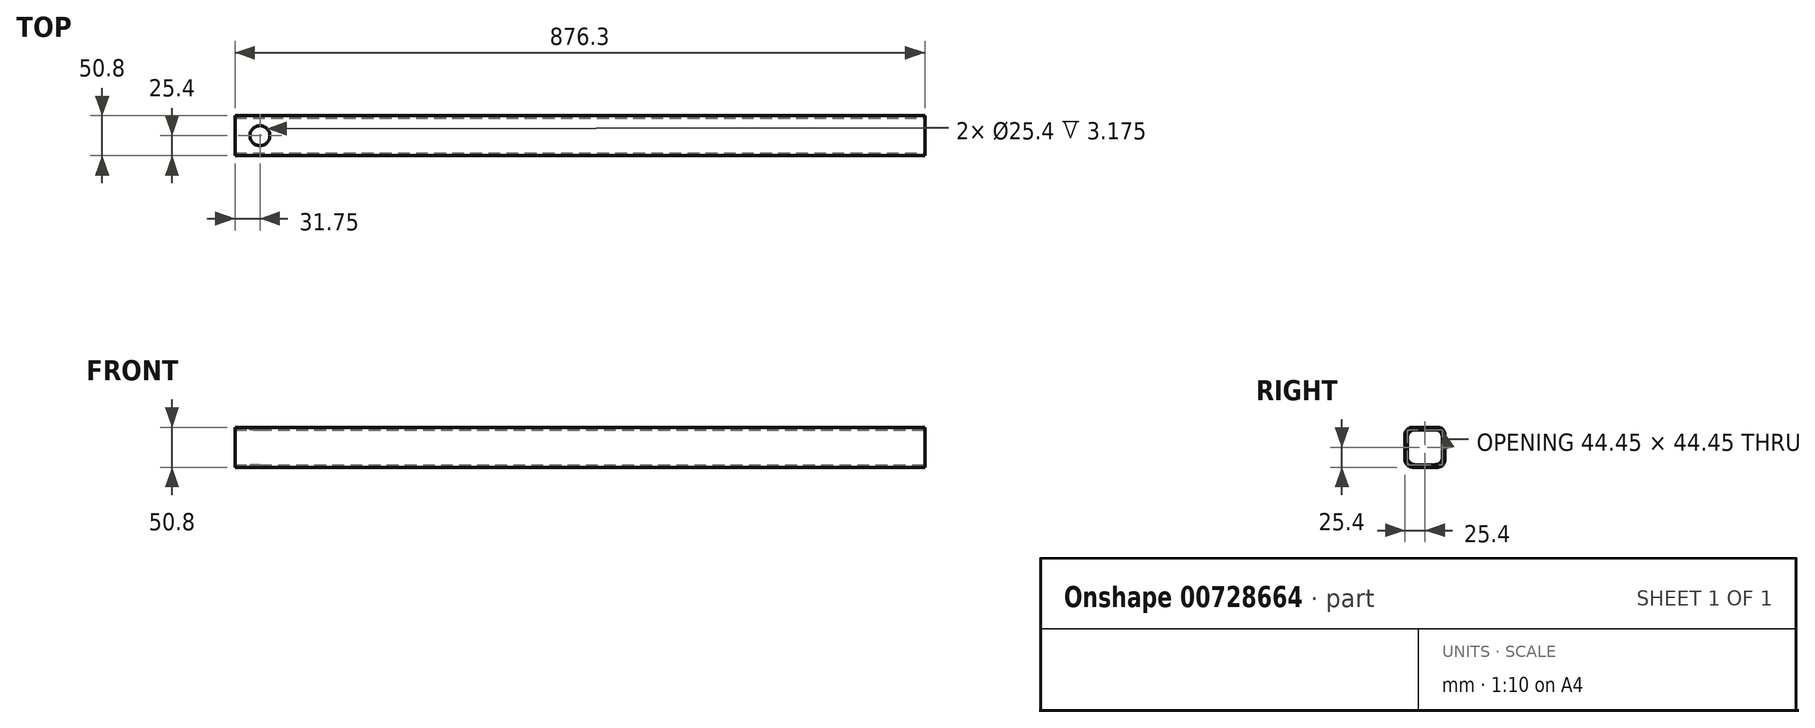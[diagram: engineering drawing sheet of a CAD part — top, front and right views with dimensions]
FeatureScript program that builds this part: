
annotation { "Feature Type Name" : "Feature", "Feature Type Description" : "" }
export const myFeature = defineFeature(function(context is Context, id is Id, definition is map)
    precondition{}
    {
        {
            var Q0;
            Q0=qCreatedBy(makeId("Right.planeOp"),FACE);
            var sketch = newSketch(context, id + "F0", { "sketchPlane" : qUnion([Q0])});
            skLineSegment(sketch, "E0.bottom", {"start": v(0, 0) * mm, "end": v(50.8, 0) * mm});
            skLineSegment(sketch, "E0.top", {"start": v(0, 50.8) * mm, "end": v(50.8, 50.8) * mm});
            skLineSegment(sketch, "E0.left", {"start": v(0, 0) * mm, "end": v(0, 50.8) * mm});
            skLineSegment(sketch, "E0.right", {"start": v(50.8, 0) * mm, "end": v(50.8, 50.8) * mm});
            skSolve(sketch);
        }
        {
            var Q0;
            Q0=qSketchRegion(id+"F0",true);
            extrude(context, id + "F1", {"entities" : qUnion([Q0]), "oppositeDirection" : true, "depth" : 876.3 * mm, "offsetDistance" : 25.4 * mm});
        }
        {
            var Q0;
            Q0=makeQuery(id+"F1.opExtrude","CAP_FACE",FACE,{"disambiguationData":[OSD([sQuery(id+"F0.wireOp",EDGE,"E0.bottom"),sQuery(id+"F0.wireOp",EDGE,"E0.top"),sQuery(id+"F0.wireOp",EDGE,"E0.left"),sQuery(id+"F0.wireOp",EDGE,"E0.right")])],"isStart":true});
            var sketch = newSketch(context, id + "F2", { "sketchPlane" : qUnion([Q0])});
            skLineSegment(sketch, "E1.0", {"start": v(3.17, 47.63) * mm, "end": v(47.63, 47.63) * mm});
            skLineSegment(sketch, "E1.1", {"start": v(3.17, 3.17) * mm, "end": v(3.17, 47.63) * mm});
            skLineSegment(sketch, "E1.2", {"start": v(3.17, 3.17) * mm, "end": v(47.63, 3.17) * mm});
            skLineSegment(sketch, "E1.3", {"start": v(47.63, 3.17) * mm, "end": v(47.63, 47.63) * mm});
            skSolve(sketch);
        }
        {
            var Q0;
            Q0=qSketchRegion(id+"F2",true);
            extrude(context, id + "F3", {"entities" : qUnion([Q0]), "operationType" : NewBodyOperationType.REMOVE, "oppositeDirection" : true, "depth" : 876.3 * mm, "offsetDistance" : 25.4 * mm});
        }
        {
            var Q0;
            Q0=makeQuery(id+"F3.boolean.opBoolean","COPY",EDGE,{"derivedFrom":makeQuery(id+"F3.opExtrude","SWEPT_EDGE",EDGE,{"disambiguationData":[OSD([sQuery(id+"F2.wireOp",EDGE,"E1.1"),sQuery(id+"F2.wireOp",EDGE,"E1.2")])]})});
            var Q1;
            Q1=makeQuery(id+"F3.boolean.opBoolean","COPY",EDGE,{"derivedFrom":makeQuery(id+"F3.opExtrude","SWEPT_EDGE",EDGE,{"disambiguationData":[OSD([sQuery(id+"F2.wireOp",EDGE,"E1.2"),sQuery(id+"F2.wireOp",EDGE,"E1.3")])]})});
            var Q2;
            Q2=makeQuery(id+"F3.boolean.opBoolean","COPY",EDGE,{"derivedFrom":makeQuery(id+"F3.opExtrude","SWEPT_EDGE",EDGE,{"disambiguationData":[OSD([sQuery(id+"F2.wireOp",EDGE,"E1.0"),sQuery(id+"F2.wireOp",EDGE,"E1.3")])]})});
            var Q3;
            Q3=makeQuery(id+"F3.boolean.opBoolean","COPY",EDGE,{"derivedFrom":makeQuery(id+"F3.opExtrude","SWEPT_EDGE",EDGE,{"disambiguationData":[OSD([sQuery(id+"F2.wireOp",EDGE,"E1.0"),sQuery(id+"F2.wireOp",EDGE,"E1.1")])]})});
            var Q4;
            Q4=makeQuery(id+"F1.opExtrude","SWEPT_EDGE",EDGE,{"disambiguationData":[OSD([sQuery(id+"F0.wireOp",EDGE,"E0.bottom"),sQuery(id+"F0.wireOp",EDGE,"E0.right")])]});
            var Q5;
            Q5=makeQuery(id+"F1.opExtrude","SWEPT_EDGE",EDGE,{"disambiguationData":[OSD([sQuery(id+"F0.wireOp",EDGE,"E0.top"),sQuery(id+"F0.wireOp",EDGE,"E0.right")])]});
            var Q6;
            Q6=makeQuery(id+"F1.opExtrude","SWEPT_EDGE",EDGE,{"disambiguationData":[OSD([sQuery(id+"F0.wireOp",EDGE,"E0.top"),sQuery(id+"F0.wireOp",EDGE,"E0.left")])]});
            var Q7;
            Q7=makeQuery(id+"F1.opExtrude","SWEPT_EDGE",EDGE,{"disambiguationData":[OSD([sQuery(id+"F0.wireOp",EDGE,"E0.bottom"),sQuery(id+"F0.wireOp",EDGE,"E0.left")])]});
            fillet(context, id + "F4", {"entities" : qUnion([Q0, Q1, Q2, Q3, Q4, Q5, Q6, Q7]), "radius" : 9.52 * mm, "tangentPropagation" : true, "allowEdgeOverflow" : false});
        }
        {
            var Q0;
            Q0=makeQuery(id+"F1.opExtrude","SWEPT_FACE",FACE,{"disambiguationData":[OSD([sQuery(id+"F0.wireOp",EDGE,"E0.top")])]});
            var sketch = newSketch(context, id + "F5", { "sketchPlane" : qUnion([Q0])});
            skLineSegment(sketch, "E2", {"start": v(0, 25.4) * mm, "end": v(-876.3, 25.4) * mm, "construction": true});
            skCircle(sketch, "E3", {"center": v(-844.55, 25.4) * mm, "radius": 12.7 * mm});
            skSolve(sketch);
        }
        {
            var Q0;
            Q0=makeQuery(id+"F5.imprint","IMPRINT",FACE,{"disambiguationData":[TD([[makeQuery(id+"F5.imprint","IMPRINT",EDGE,{"derivedFrom":sQuery(id+"F5.wireOp",EDGE,"E3")}),1.0]])]});
            extrude(context, id + "F6", {"entities" : qUnion([Q0]), "operationType" : NewBodyOperationType.REMOVE, "oppositeDirection" : true, "depth" : 50.8 * mm, "offsetDistance" : 25.4 * mm});
        }
    });
